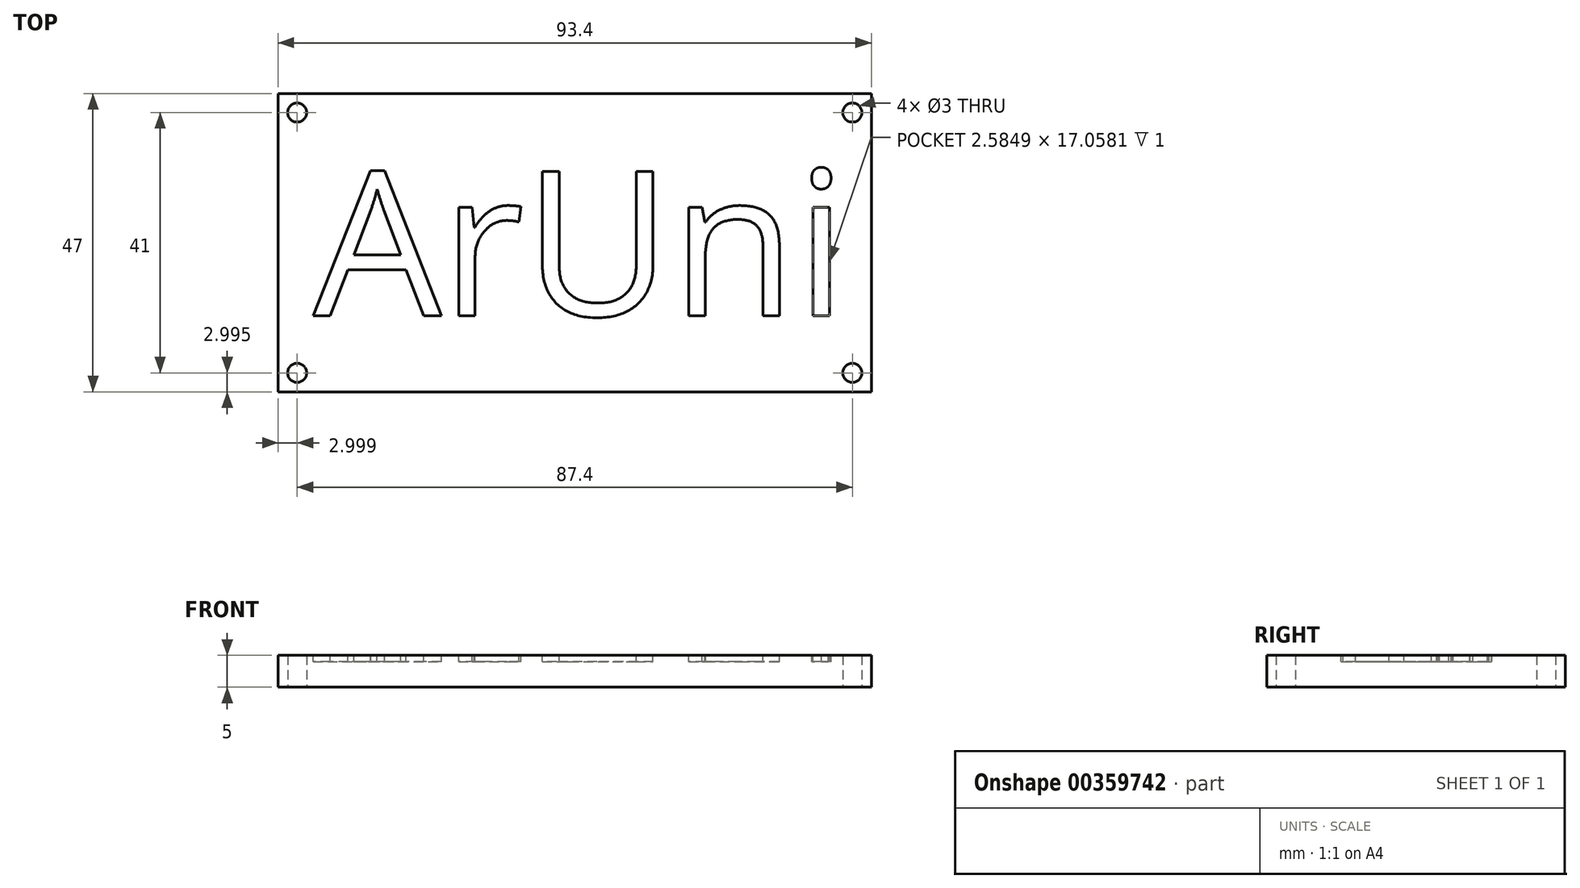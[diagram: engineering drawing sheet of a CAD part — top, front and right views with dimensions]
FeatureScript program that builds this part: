
annotation { "Feature Type Name" : "Feature", "Feature Type Description" : "" }
export const myFeature = defineFeature(function(context is Context, id is Id, definition is map)
    precondition{}
    {
        {
            var Q0;
            Q0=qCreatedBy(makeId("Top.planeOp"),FACE);
            var sketch = newSketch(context, id + "F0", { "sketchPlane" : qUnion([Q0])});
            skLineSegment(sketch, "E0.bottom", {"start": v(-69.62, -33.05) * mm, "end": v(23.78, -33.05) * mm});
            skLineSegment(sketch, "E0.top", {"start": v(-69.62, 13.95) * mm, "end": v(23.78, 13.95) * mm});
            skLineSegment(sketch, "E0.left", {"start": v(-69.62, -33.05) * mm, "end": v(-69.62, 13.95) * mm});
            skLineSegment(sketch, "E0.right", {"start": v(23.78, -33.05) * mm, "end": v(23.78, 13.95) * mm});
            skCircle(sketch, "E1", {"center": v(-66.62, 10.95) * mm, "radius": 1.5 * mm});
            skCircle(sketch, "E2", {"center": v(20.78, 10.95) * mm, "radius": 1.5 * mm});
            skCircle(sketch, "E3", {"center": v(20.78, -30.05) * mm, "radius": 1.5 * mm});
            skCircle(sketch, "E4", {"center": v(-66.62, -30.05) * mm, "radius": 1.5 * mm});
            skSolve(sketch);
        }
        {
            var Q0;
            Q0=makeQuery(id+"F0.imprint","IMPRINT",FACE,{"disambiguationData":[TD([[makeQuery(id+"F0.imprint","IMPRINT",EDGE,{"derivedFrom":sQuery(id+"F0.wireOp",EDGE,"E0.bottom")}),1.0]])]});
            var Q1;
            Q1=makeQuery(id+"F0.imprint","IMPRINT",FACE,{"disambiguationData":[TD([[makeQuery(id+"F0.imprint","IMPRINT",EDGE,{"derivedFrom":sQuery(id+"F0.wireOp",EDGE,"69849541-1728-4e11-86fb-5258966d240f.sketch_text.stroke-8")}),1.0]])]});
            var Q2;
            Q2=makeQuery(id+"F0.imprint","IMPRINT",FACE,{"disambiguationData":[TD([[makeQuery(id+"F0.imprint","IMPRINT",EDGE,{"derivedFrom":sQuery(id+"F0.wireOp",EDGE,"69849541-1728-4e11-86fb-5258966d240f.sketch_text.stroke-0")}),-1.0]])]});
            var Q3;
            Q3=makeQuery(id+"F0.imprint","IMPRINT",FACE,{"disambiguationData":[TD([[makeQuery(id+"F0.imprint","IMPRINT",EDGE,{"derivedFrom":sQuery(id+"F0.wireOp",EDGE,"69849541-1728-4e11-86fb-5258966d240f.sketch_text.stroke-13")}),-1.0]])]});
            var Q4;
            Q4=makeQuery(id+"F0.imprint","IMPRINT",FACE,{"disambiguationData":[TD([[makeQuery(id+"F0.imprint","IMPRINT",EDGE,{"derivedFrom":sQuery(id+"F0.wireOp",EDGE,"69849541-1728-4e11-86fb-5258966d240f.sketch_text.stroke-26")}),-1.0]])]});
            var Q5;
            Q5=makeQuery(id+"F0.imprint","IMPRINT",FACE,{"disambiguationData":[TD([[makeQuery(id+"F0.imprint","IMPRINT",EDGE,{"derivedFrom":sQuery(id+"F0.wireOp",EDGE,"69849541-1728-4e11-86fb-5258966d240f.sketch_text.stroke-40")}),-1.0]])]});
            var Q6;
            Q6=makeQuery(id+"F0.imprint","IMPRINT",FACE,{"disambiguationData":[TD([[makeQuery(id+"F0.imprint","IMPRINT",EDGE,{"derivedFrom":sQuery(id+"F0.wireOp",EDGE,"69849541-1728-4e11-86fb-5258966d240f.sketch_text.stroke-57")}),-1.0]])]});
            var Q7;
            Q7=makeQuery(id+"F0.imprint","IMPRINT",FACE,{"disambiguationData":[TD([[makeQuery(id+"F0.imprint","IMPRINT",EDGE,{"derivedFrom":sQuery(id+"F0.wireOp",EDGE,"69849541-1728-4e11-86fb-5258966d240f.sketch_text.stroke-61")}),-1.0]])]});
            extrude(context, id + "F1", {"entities" : qUnion([Q0, Q1, Q2, Q3, Q4, Q5, Q6, Q7]), "depth" : 5 * mm});
        }
        {
            var Q0;
            Q0=makeQuery(id+"F1.opExtrude","CAP_FACE",FACE,{"disambiguationData":[OSD([sQuery(id+"F0.wireOp",EDGE,"E0.bottom"),sQuery(id+"F0.wireOp",EDGE,"E0.top"),sQuery(id+"F0.wireOp",EDGE,"E0.left"),sQuery(id+"F0.wireOp",EDGE,"E0.right"),sQuery(id+"F0.wireOp",EDGE,"E1"),sQuery(id+"F0.wireOp",EDGE,"E2"),sQuery(id+"F0.wireOp",EDGE,"E3"),sQuery(id+"F0.wireOp",EDGE,"E4")])],"isStart":false});
            var sketch = newSketch(context, id + "F2", { "sketchPlane" : qUnion([Q0])});
            skLineSegment(sketch, "E5.0", {"start": v(-69.62, -33.05) * mm, "end": v(23.78, -33.05) * mm});
            skLineSegment(sketch, "E5.1", {"start": v(-69.62, 13.95) * mm, "end": v(23.78, 13.95) * mm});
            skLineSegment(sketch, "E5.2", {"start": v(-69.62, -33.05) * mm, "end": v(-69.62, 13.95) * mm});
            skLineSegment(sketch, "E5.3", {"start": v(23.78, -33.05) * mm, "end": v(23.78, 13.95) * mm});
            skCircle(sketch, "E5.4", {"center": v(-66.62, 10.95) * mm, "radius": 1.5 * mm});
            skCircle(sketch, "E5.5", {"center": v(20.78, 10.95) * mm, "radius": 1.5 * mm});
            skCircle(sketch, "E5.6", {"center": v(20.78, -30.05) * mm, "radius": 1.5 * mm});
            skCircle(sketch, "E5.7", {"center": v(-66.62, -30.05) * mm, "radius": 1.5 * mm});
            skText(sketch, "E6", { "text": "ArUni", "fontName": "OpenSans-Regular.ttf"});
            const initialGuessF2  = {"E6": [-0.0641, -0.02106, 1, 0, 0.02295]};
            skSetInitialGuess(sketch, initialGuessF2);
            skSolve(sketch);
        }
        {
            var Q0;
            Q0=makeQuery(id+"F2.imprint","IMPRINT",FACE,{"disambiguationData":[TD([[makeQuery(id+"F2.imprint","IMPRINT",EDGE,{"derivedFrom":sQuery(id+"F2.wireOp",EDGE,"E6.sketch_text.stroke-0")}),-1.0]])]});
            var Q1;
            Q1=makeQuery(id+"F2.imprint","IMPRINT",FACE,{"disambiguationData":[TD([[makeQuery(id+"F2.imprint","IMPRINT",EDGE,{"derivedFrom":sQuery(id+"F2.wireOp",EDGE,"E6.sketch_text.stroke-13")}),-1.0]])]});
            var Q2;
            Q2=makeQuery(id+"F2.imprint","IMPRINT",FACE,{"disambiguationData":[TD([[makeQuery(id+"F2.imprint","IMPRINT",EDGE,{"derivedFrom":sQuery(id+"F2.wireOp",EDGE,"E6.sketch_text.stroke-26")}),-1.0]])]});
            var Q3;
            Q3=makeQuery(id+"F2.imprint","IMPRINT",FACE,{"disambiguationData":[TD([[makeQuery(id+"F2.imprint","IMPRINT",EDGE,{"derivedFrom":sQuery(id+"F2.wireOp",EDGE,"E6.sketch_text.stroke-40")}),-1.0]])]});
            var Q4;
            Q4=makeQuery(id+"F2.imprint","IMPRINT",FACE,{"disambiguationData":[TD([[makeQuery(id+"F2.imprint","IMPRINT",EDGE,{"derivedFrom":sQuery(id+"F2.wireOp",EDGE,"E6.sketch_text.stroke-57")}),-1.0]])]});
            var Q5;
            Q5=makeQuery(id+"F2.imprint","IMPRINT",FACE,{"disambiguationData":[TD([[makeQuery(id+"F2.imprint","IMPRINT",EDGE,{"derivedFrom":sQuery(id+"F2.wireOp",EDGE,"E6.sketch_text.stroke-61")}),-1.0]])]});
            extrude(context, id + "F3", {"entities" : qUnion([Q0, Q1, Q2, Q3, Q4, Q5]), "operationType" : NewBodyOperationType.REMOVE, "oppositeDirection" : true, "depth" : 1 * mm});
        }
    });
